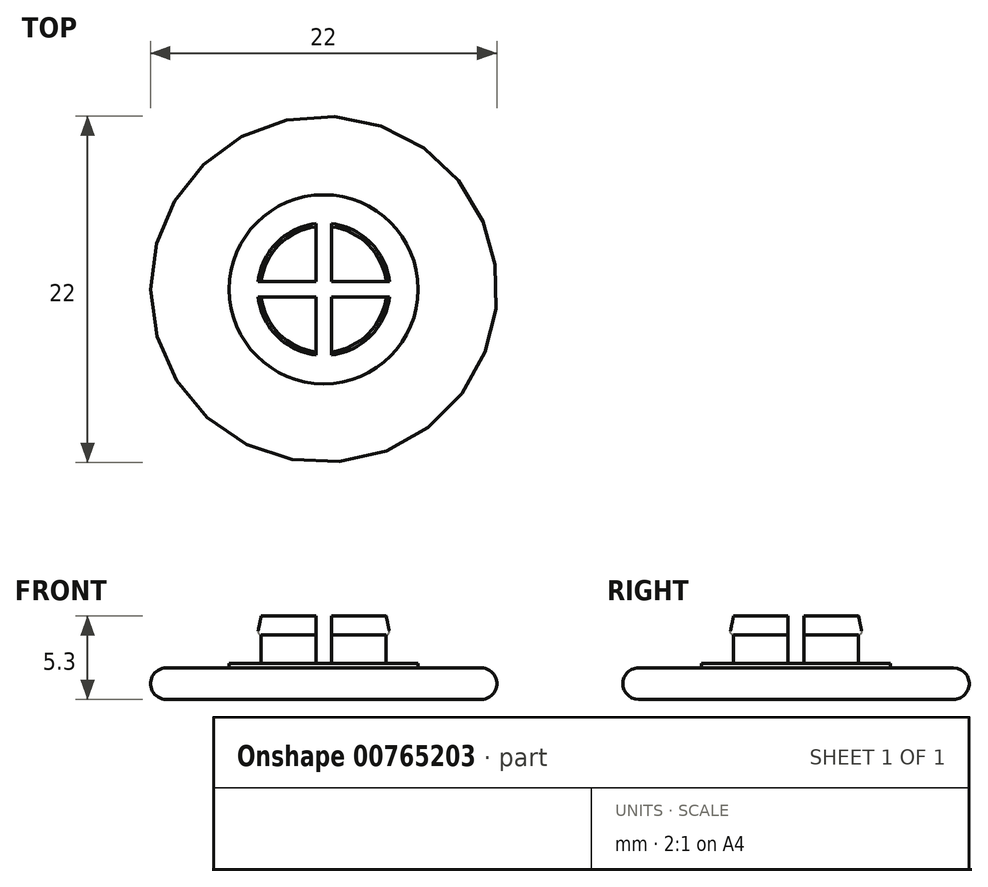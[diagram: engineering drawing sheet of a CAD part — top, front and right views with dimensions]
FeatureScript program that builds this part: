
annotation { "Feature Type Name" : "Feature", "Feature Type Description" : "" }
export const myFeature = defineFeature(function(context is Context, id is Id, definition is map)
    precondition{}
    {
        {
            var Q0;
            Q0=qCreatedBy(makeId("Front.planeOp"),FACE);
            var sketch = newSketch(context, id + "F0", { "sketchPlane" : qUnion([Q0])});
            skLineSegment(sketch, "E0.bottom", {"start": v(0, 0) * mm, "end": v(-10, 0) * mm});
            skLineSegment(sketch, "E0.top", {"start": v(-6, 2) * mm, "end": v(-10, 2) * mm});
            skLineSegment(sketch, "E0.left", {"start": v(0, 0) * mm, "end": v(0, 2) * mm});
            skLineSegment(sketch, "E1.top", {"start": v(-4, 2.3) * mm, "end": v(-6, 2.3) * mm});
            skLineSegment(sketch, "E1.left", {"start": v(0, 2) * mm, "end": v(0, 2.3) * mm});
            skLineSegment(sketch, "E1.right", {"start": v(-6, 2) * mm, "end": v(-6, 2.3) * mm});
            skLineSegment(sketch, "E2.top", {"start": v(0, 5.3) * mm, "end": v(-4, 5.3) * mm});
            skLineSegment(sketch, "E2.left", {"start": v(0, 2.3) * mm, "end": v(0, 5.3) * mm});
            skLineSegment(sketch, "E2.right", {"start": v(-4, 2.3) * mm, "end": v(-4, 4.1) * mm});
            skArc(sketch, "E3", {"start": v(-10, 2) * mm, "mid": v(-11, 1) * mm, "end": v(-10, 0) * mm});
            skArc(sketch, "E4", {"start": v(-4.2, 4.34) * mm, "mid": v(-4.15, 4.17) * mm, "end": v(-4, 4.1) * mm});
            skLineSegment(sketch, "E5", {"start": v(-4, 5.3) * mm, "end": v(-4.2, 4.34) * mm});
            skSolve(sketch);
        }
        {
            var Q0;
            Q0=makeQuery(id+"F0.imprint","IMPRINT",FACE,{"disambiguationData":[TD([[makeQuery(id+"F0.imprint","IMPRINT",EDGE,{"derivedFrom":sQuery(id+"F0.wireOp",EDGE,"E0.bottom")}),-1.0]])]});
            var Q1;
            Q1=sQuery(id+"F0.wireOp",EDGE,"E0.left");
            revolve(context, id + "F1", {"surfaceOperationType" : NewSurfaceOperationType.NEW, "entities" : qUnion([Q0]), "axis" : qUnion([Q1]), "revolveType" : RevolveType.FULL});
        }
        {
            var Q0;
            Q0=makeQuery(id+"F1.opRevolve","SWEPT_FACE",FACE,{"disambiguationData":[OSD([sQuery(id+"F0.wireOp",EDGE,"E2.top")])]});
            var sketch = newSketch(context, id + "F2", { "sketchPlane" : qUnion([Q0])});
            skLineSegment(sketch, "E6.bottom", {"start": v(-5.5, 0.5) * mm, "end": v(-0.5, 0.5) * mm});
            skLineSegment(sketch, "E6.top", {"start": v(-5.5, -0.5) * mm, "end": v(-0.5, -0.5) * mm});
            skLineSegment(sketch, "E6.left", {"start": v(-5.5, 0.5) * mm, "end": v(-5.5, -0.5) * mm});
            skLineSegment(sketch, "E6.right", {"start": v(5.5, 0.5) * mm, "end": v(5.5, -0.5) * mm});
            skPoint(sketch, "E6.middle", {"position": v(0, 0) * mm});
            skLineSegment(sketch, "E7.bottom", {"start": v(-0.5, 5.5) * mm, "end": v(0.5, 5.5) * mm});
            skLineSegment(sketch, "E7.top", {"start": v(-0.5, -5.5) * mm, "end": v(0.5, -5.5) * mm});
            skLineSegment(sketch, "E7.left", {"start": v(-0.5, 5.5) * mm, "end": v(-0.5, 0.5) * mm});
            skLineSegment(sketch, "E7.right", {"start": v(0.5, 5.5) * mm, "end": v(0.5, 0.5) * mm});
            skLineSegment(sketch, "E8.trimOffspring", {"start": v(0.5, 0.5) * mm, "end": v(5.5, 0.5) * mm});
            skLineSegment(sketch, "E9.trimOffspring", {"start": v(-0.5, -0.5) * mm, "end": v(-0.5, -5.5) * mm});
            skLineSegment(sketch, "E10.trimOffspring", {"start": v(0.5, -0.5) * mm, "end": v(5.5, -0.5) * mm});
            skLineSegment(sketch, "E11.trimOffspring", {"start": v(0.5, -0.5) * mm, "end": v(0.5, -5.5) * mm});
            skSolve(sketch);
        }
        {
            var Q0;
            Q0 = qSketchRegion(id + "F2", true);
            extrude(context, id + "F3", {"entities" : qUnion([Q0]), "operationType" : NewBodyOperationType.REMOVE, "oppositeDirection" : true, "depth" : 3 * mm, "offsetDistance" : 25 * mm});
        }
    });
